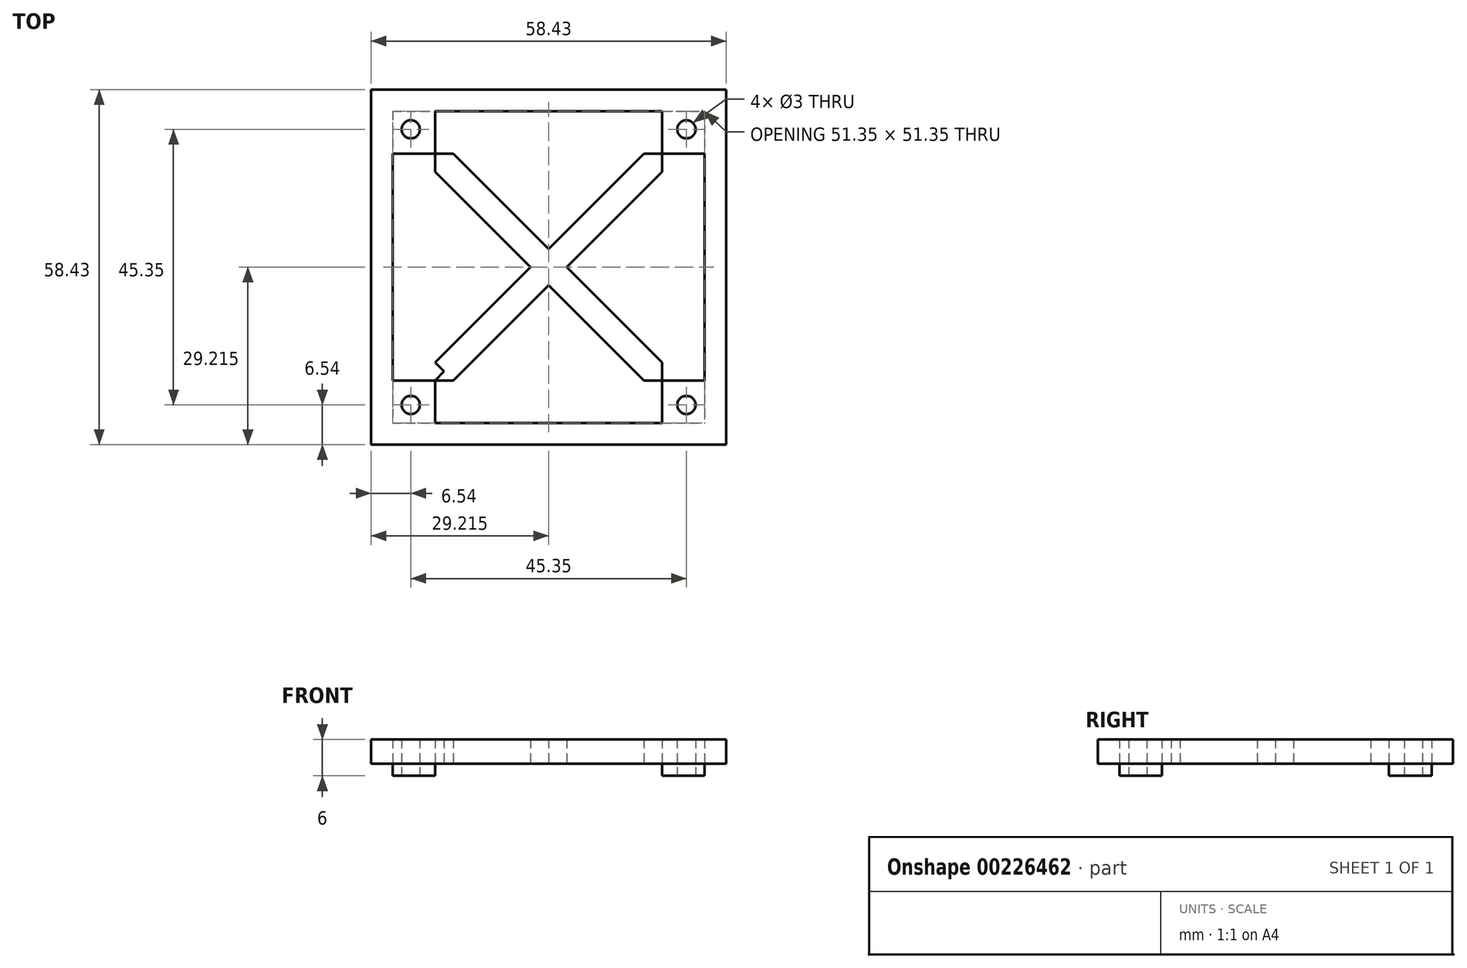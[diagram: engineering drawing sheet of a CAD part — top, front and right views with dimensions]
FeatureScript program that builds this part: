
annotation { "Feature Type Name" : "Feature", "Feature Type Description" : "" }
export const myFeature = defineFeature(function(context is Context, id is Id, definition is map)
    precondition{}
    {
        {
            var Q0;
            Q0=qCreatedBy(makeId("Top.planeOp"),FACE);
            var sketch = newSketch(context, id + "F0", { "sketchPlane" : qUnion([Q0])});
            skLineSegment(sketch, "E0.bottom", {"start": v(0, 0) * mm, "end": v(51.35, 0) * mm});
            skLineSegment(sketch, "E0.top", {"start": v(0, -51.35) * mm, "end": v(51.35, -51.35) * mm});
            skLineSegment(sketch, "E0.left", {"start": v(0, 0) * mm, "end": v(0, -51.35) * mm});
            skLineSegment(sketch, "E0.right", {"start": v(51.35, 0) * mm, "end": v(51.35, -51.35) * mm});
            skCircle(sketch, "E1", {"center": v(3, -3) * mm, "radius": 1.5 * mm});
            skCircle(sketch, "E2", {"center": v(48.35, -3) * mm, "radius": 1.5 * mm});
            skCircle(sketch, "E3", {"center": v(48.35, -48.35) * mm, "radius": 1.5 * mm});
            skCircle(sketch, "E4", {"center": v(3, -48.35) * mm, "radius": 1.5 * mm});
            skLineSegment(sketch, "E5", {"start": v(0, -3) * mm, "end": v(1.5, -3) * mm});
            skLineSegment(sketch, "E6", {"start": v(51.35, -3) * mm, "end": v(49.85, -3) * mm});
            skLineSegment(sketch, "E7", {"start": v(3, -1.5) * mm, "end": v(3, 0) * mm});
            skLineSegment(sketch, "E8", {"start": v(3, -51.35) * mm, "end": v(3, -48.35) * mm});
            skLineSegment(sketch, "E9", {"start": v(3, -48.35) * mm, "end": v(0, -48.35) * mm});
            skLineSegment(sketch, "E10", {"start": v(48.35, -48.35) * mm, "end": v(51.35, -48.35) * mm});
            skLineSegment(sketch, "E11", {"start": v(48.35, -48.35) * mm, "end": v(48.35, -51.35) * mm});
            skLineSegment(sketch, "E12", {"start": v(1.5, -3) * mm, "end": v(3, -3) * mm});
            skLineSegment(sketch, "E13", {"start": v(3, -3) * mm, "end": v(3, -1.5) * mm});
            skLineSegment(sketch, "E14", {"start": v(48.35, -3) * mm, "end": v(49.85, -3) * mm});
            skLineSegment(sketch, "E15", {"start": v(48.35, -3) * mm, "end": v(48.35, 0) * mm});
            skLineSegment(sketch, "E16", {"start": v(3, -3) * mm, "end": v(0, 0) * mm});
            skLineSegment(sketch, "E17", {"start": v(0, 0) * mm, "end": v(-3.54, 3.54) * mm});
            skLineSegment(sketch, "E18", {"start": v(51.35, 0) * mm, "end": v(54.89, 3.54) * mm});
            skLineSegment(sketch, "E19", {"start": v(51.35, -51.35) * mm, "end": v(54.89, -54.89) * mm});
            skLineSegment(sketch, "E20", {"start": v(54.89, -54.89) * mm, "end": v(-3.54, -54.89) * mm});
            skLineSegment(sketch, "E21", {"start": v(-3.54, -54.89) * mm, "end": v(0, -51.35) * mm});
            skLineSegment(sketch, "E22", {"start": v(-3.54, -54.89) * mm, "end": v(-3.54, 3.54) * mm});
            skLineSegment(sketch, "E23", {"start": v(54.89, 3.54) * mm, "end": v(-3.54, 3.54) * mm});
            skLineSegment(sketch, "E24", {"start": v(54.89, 3.54) * mm, "end": v(54.89, -54.89) * mm});
            skLineSegment(sketch, "E25.bottom", {"start": v(0, -51.35) * mm, "end": v(7, -51.35) * mm});
            skLineSegment(sketch, "E25.top", {"start": v(0, -44.35) * mm, "end": v(7, -44.35) * mm});
            skLineSegment(sketch, "E25.left", {"start": v(0, -51.35) * mm, "end": v(0, -44.35) * mm});
            skLineSegment(sketch, "E25.right", {"start": v(7, -51.35) * mm, "end": v(7, -44.35) * mm});
            skLineSegment(sketch, "E26.bottom", {"start": v(51.35, -51.35) * mm, "end": v(44.35, -51.35) * mm});
            skLineSegment(sketch, "E26.top", {"start": v(51.35, -44.35) * mm, "end": v(44.35, -44.35) * mm});
            skLineSegment(sketch, "E26.left", {"start": v(51.35, -51.35) * mm, "end": v(51.35, -44.35) * mm});
            skLineSegment(sketch, "E26.right", {"start": v(44.35, -51.35) * mm, "end": v(44.35, -44.35) * mm});
            skLineSegment(sketch, "E27.bottom", {"start": v(51.35, 0) * mm, "end": v(44.35, 0) * mm});
            skLineSegment(sketch, "E27.top", {"start": v(51.35, -7) * mm, "end": v(44.35, -7) * mm});
            skLineSegment(sketch, "E27.left", {"start": v(51.35, 0) * mm, "end": v(51.35, -7) * mm});
            skLineSegment(sketch, "E27.right", {"start": v(44.35, 0) * mm, "end": v(44.35, -7) * mm});
            skLineSegment(sketch, "E28.bottom", {"start": v(0, 0) * mm, "end": v(7, 0) * mm});
            skLineSegment(sketch, "E28.top", {"start": v(0, -7) * mm, "end": v(7, -7) * mm});
            skLineSegment(sketch, "E28.left", {"start": v(0, 0) * mm, "end": v(0, -7) * mm});
            skLineSegment(sketch, "E28.right", {"start": v(7, 0) * mm, "end": v(7, -7) * mm});
            skLineSegment(sketch, "E29", {"start": v(7, -44.35) * mm, "end": v(7, -7) * mm});
            skLineSegment(sketch, "E30", {"start": v(44.35, -7) * mm, "end": v(7, -7) * mm});
            skLineSegment(sketch, "E31", {"start": v(44.35, -7) * mm, "end": v(44.35, -44.35) * mm});
            skLineSegment(sketch, "E32", {"start": v(44.35, -44.35) * mm, "end": v(7, -44.35) * mm});
            skLineSegment(sketch, "E33", {"start": v(7, -44.35) * mm, "end": v(44.35, -7) * mm});
            skLineSegment(sketch, "E34", {"start": v(44.35, -44.35) * mm, "end": v(7, -7) * mm});
            skLineSegment(sketch, "E35", {"start": v(10, -44.35) * mm, "end": v(44.35, -10) * mm});
            skLineSegment(sketch, "E36", {"start": v(44.35, -10) * mm, "end": v(41.35, -7) * mm});
            skLineSegment(sketch, "E37", {"start": v(41.35, -7) * mm, "end": v(7, -41.35) * mm});
            skLineSegment(sketch, "E38", {"start": v(7, -10) * mm, "end": v(41.35, -44.35) * mm});
            skLineSegment(sketch, "E39", {"start": v(41.35, -44.35) * mm, "end": v(44.35, -41.35) * mm});
            skLineSegment(sketch, "E40", {"start": v(44.35, -41.35) * mm, "end": v(10, -7) * mm});
            skLineSegment(sketch, "E41", {"start": v(10, -7) * mm, "end": v(7, -10) * mm});
            skLineSegment(sketch, "E42", {"start": v(7, -41.35) * mm, "end": v(10, -44.35) * mm});
            skLineSegment(sketch, "E43", {"start": v(42.85, -8.5) * mm, "end": v(41.35, -7) * mm});
            skLineSegment(sketch, "E44", {"start": v(7, -41.35) * mm, "end": v(7, -44.35) * mm});
            skSolve(sketch);
        }
        {
            var Q0;
            {var subQ2=sQuery(id+"F0.wireOp",EDGE,"E0.top");Q0=makeQuery(id+"F0.imprint","IMPRINT",FACE,{"disambiguationData":[TD([[makeQuery(id+"F0.imprint","IMPRINT",EDGE,{"derivedFrom":subQ2}),-1.0]])]});}
            var Q1;
            Q1=makeQuery(id+"F0.imprint","IMPRINT",FACE,{"disambiguationData":[TD([[makeQuery(id+"F0.imprint","IMPRINT",EDGE,{"derivedFrom":sQuery(id+"F0.wireOp",EDGE,"E0.left")}),1.0]])]});
            var Q2;
            Q2=makeQuery(id+"F0.imprint","IMPRINT",FACE,{"disambiguationData":[TD([[makeQuery(id+"F0.imprint","IMPRINT",EDGE,{"derivedFrom":sQuery(id+"F0.wireOp",EDGE,"E0.top")}),1.0]])]});
            var Q3;
            {var subQ9=sQuery(id+"F0.wireOp",EDGE,"E25.top");Q3=makeQuery(id+"F0.imprint","IMPRINT",FACE,{"disambiguationData":[TD([[makeQuery(id+"F0.imprint","IMPRINT",EDGE,{"derivedFrom":subQ9}),-1.0]])]});}
            var Q4;
            {var subQ1=sQuery(id+"F0.wireOp",EDGE,"E8");var subQ7=sQuery(id+"F0.wireOp",EDGE,"E4");var subQ9=makeQuery(id+"F0.imprint","INTERSECT",VERTEX,{"derivedFrom":[subQ7,subQ1]});Q4=makeQuery(id+"F0.imprint","IMPRINT",FACE,{"disambiguationData":[TD([[makeQuery(id+"F0.imprint","IMPRINT",EDGE,{"disambiguationData":[TD([[subQ9,1.0]])],"derivedFrom":subQ7}),-1.0]])]});}
            var Q5;
            {var subQ1=sQuery(id+"F0.wireOp",EDGE,"E0.left");Q5=makeQuery(id+"F0.imprint","IMPRINT",FACE,{"disambiguationData":[TD([[makeQuery(id+"F0.imprint","IMPRINT",EDGE,{"derivedFrom":subQ1}),-1.0]])]});}
            var Q6;
            {var subQ4=sQuery(id+"F0.wireOp",EDGE,"E5");Q6=makeQuery(id+"F0.imprint","IMPRINT",FACE,{"disambiguationData":[TD([[makeQuery(id+"F0.imprint","IMPRINT",EDGE,{"derivedFrom":subQ4}),-1.0]])]});}
            var Q7;
            {var subQ0=sQuery(id+"F0.wireOp",EDGE,"E7");Q7=makeQuery(id+"F0.imprint","IMPRINT",FACE,{"disambiguationData":[TD([[makeQuery(id+"F0.imprint","IMPRINT",EDGE,{"derivedFrom":subQ0}),1.0]])]});}
            var Q8;
            {var subQ0=sQuery(id+"F0.wireOp",EDGE,"E5");Q8=makeQuery(id+"F0.imprint","IMPRINT",FACE,{"disambiguationData":[TD([[makeQuery(id+"F0.imprint","IMPRINT",EDGE,{"derivedFrom":subQ0}),1.0]])]});}
            var Q9;
            {var subQ2=sQuery(id+"F0.wireOp",EDGE,"E0.bottom");Q9=makeQuery(id+"F0.imprint","IMPRINT",FACE,{"disambiguationData":[TD([[makeQuery(id+"F0.imprint","IMPRINT",EDGE,{"derivedFrom":subQ2}),1.0]])]});}
            var Q10;
            Q10=makeQuery(id+"F0.imprint","IMPRINT",FACE,{"disambiguationData":[TD([[makeQuery(id+"F0.imprint","IMPRINT",EDGE,{"derivedFrom":sQuery(id+"F0.wireOp",EDGE,"E0.bottom")}),-1.0]])]});
            var Q11;
            {var subQ4=sQuery(id+"F0.wireOp",EDGE,"E6");Q11=makeQuery(id+"F0.imprint","IMPRINT",FACE,{"disambiguationData":[TD([[makeQuery(id+"F0.imprint","IMPRINT",EDGE,{"derivedFrom":subQ4}),1.0]])]});}
            var Q12;
            {var subQ5=sQuery(id+"F0.wireOp",EDGE,"E6");Q12=makeQuery(id+"F0.imprint","IMPRINT",FACE,{"disambiguationData":[TD([[makeQuery(id+"F0.imprint","IMPRINT",EDGE,{"derivedFrom":subQ5}),-1.0]])]});}
            var Q13;
            {var subQ4=sQuery(id+"F0.wireOp",EDGE,"E0.right");Q13=makeQuery(id+"F0.imprint","IMPRINT",FACE,{"disambiguationData":[TD([[makeQuery(id+"F0.imprint","IMPRINT",EDGE,{"derivedFrom":subQ4}),1.0]])]});}
            var Q14;
            Q14=makeQuery(id+"F0.imprint","IMPRINT",FACE,{"disambiguationData":[TD([[makeQuery(id+"F0.imprint","IMPRINT",EDGE,{"derivedFrom":sQuery(id+"F0.wireOp",EDGE,"E0.right")}),-1.0]])]});
            var Q15;
            {var subQ3=sQuery(id+"F0.wireOp",EDGE,"E3");var subQ7=sQuery(id+"F0.wireOp",EDGE,"E10");var subQ9=makeQuery(id+"F0.imprint","INTERSECT",VERTEX,{"derivedFrom":[subQ3,subQ7]});Q15=makeQuery(id+"F0.imprint","IMPRINT",FACE,{"disambiguationData":[TD([[makeQuery(id+"F0.imprint","IMPRINT",EDGE,{"disambiguationData":[TD([[subQ9,1.0]])],"derivedFrom":subQ3}),-1.0]])]});}
            var Q16;
            {var subQ10=sQuery(id+"F0.wireOp",EDGE,"E26.top");Q16=makeQuery(id+"F0.imprint","IMPRINT",FACE,{"disambiguationData":[TD([[makeQuery(id+"F0.imprint","IMPRINT",EDGE,{"derivedFrom":subQ10}),1.0]])]});}
            var Q17;
            {var subQ0=sQuery(id+"F0.wireOp",EDGE,"E44");Q17=makeQuery(id+"F0.imprint","IMPRINT",FACE,{"disambiguationData":[TD([[makeQuery(id+"F0.imprint","IMPRINT",EDGE,{"derivedFrom":subQ0}),1.0]])]});}
            var Q18;
            {var subQ0=sQuery(id+"F0.wireOp",EDGE,"E33");var subQ3=sQuery(id+"F0.wireOp",EDGE,"E42");var subQ5=makeQuery(id+"F0.imprint","INTERSECT",VERTEX,{"derivedFrom":[subQ0,subQ3]});Q18=makeQuery(id+"F0.imprint","IMPRINT",FACE,{"disambiguationData":[TD([[makeQuery(id+"F0.imprint","IMPRINT",EDGE,{"disambiguationData":[TD([[subQ5,-1.0]])],"derivedFrom":subQ3}),-1.0]])]});}
            var Q19;
            {var subQ0=sQuery(id+"F0.wireOp",EDGE,"E42");var subQ1=sQuery(id+"F0.wireOp",EDGE,"E33");var subQ2=makeQuery(id+"F0.imprint","INTERSECT",VERTEX,{"derivedFrom":[subQ1,subQ0]});Q19=makeQuery(id+"F0.imprint","IMPRINT",FACE,{"disambiguationData":[TD([[makeQuery(id+"F0.imprint","IMPRINT",EDGE,{"disambiguationData":[TD([[subQ2,-1.0]])],"derivedFrom":subQ1}),-1.0]])]});}
            var Q20;
            {var subQ0=sQuery(id+"F0.wireOp",EDGE,"E42");var subQ1=sQuery(id+"F0.wireOp",EDGE,"E33");var subQ2=makeQuery(id+"F0.imprint","INTERSECT",VERTEX,{"derivedFrom":[subQ1,subQ0]});Q20=makeQuery(id+"F0.imprint","IMPRINT",FACE,{"disambiguationData":[TD([[makeQuery(id+"F0.imprint","IMPRINT",EDGE,{"disambiguationData":[TD([[subQ2,-1.0]])],"derivedFrom":subQ1}),1.0]])]});}
            var Q21;
            {var subQ0=sQuery(id+"F0.wireOp",EDGE,"E37");var subQ1=sQuery(id+"F0.wireOp",EDGE,"E34");var subQ2=makeQuery(id+"F0.imprint","INTERSECT",VERTEX,{"derivedFrom":[subQ1,subQ0]});Q21=makeQuery(id+"F0.imprint","IMPRINT",FACE,{"disambiguationData":[TD([[makeQuery(id+"F0.imprint","IMPRINT",EDGE,{"disambiguationData":[TD([[subQ2,-1.0]])],"derivedFrom":subQ1}),1.0]])]});}
            var Q22;
            {var subQ0=sQuery(id+"F0.wireOp",EDGE,"E37");var subQ1=sQuery(id+"F0.wireOp",EDGE,"E34");var subQ2=makeQuery(id+"F0.imprint","INTERSECT",VERTEX,{"derivedFrom":[subQ1,subQ0]});Q22=makeQuery(id+"F0.imprint","IMPRINT",FACE,{"disambiguationData":[TD([[makeQuery(id+"F0.imprint","IMPRINT",EDGE,{"disambiguationData":[TD([[subQ2,-1.0]])],"derivedFrom":subQ1}),-1.0]])]});}
            var Q23;
            {var subQ0=sQuery(id+"F0.wireOp",EDGE,"E34");var subQ1=sQuery(id+"F0.wireOp",EDGE,"E33");var subQ2=makeQuery(id+"F0.imprint","INTERSECT",VERTEX,{"derivedFrom":[subQ1,subQ0]});Q23=makeQuery(id+"F0.imprint","IMPRINT",FACE,{"disambiguationData":[TD([[makeQuery(id+"F0.imprint","IMPRINT",EDGE,{"disambiguationData":[TD([[subQ2,-1.0]])],"derivedFrom":subQ1}),1.0]])]});}
            var Q24;
            {var subQ0=sQuery(id+"F0.wireOp",EDGE,"E34");var subQ1=sQuery(id+"F0.wireOp",EDGE,"E33");var subQ2=makeQuery(id+"F0.imprint","INTERSECT",VERTEX,{"derivedFrom":[subQ1,subQ0]});Q24=makeQuery(id+"F0.imprint","IMPRINT",FACE,{"disambiguationData":[TD([[makeQuery(id+"F0.imprint","IMPRINT",EDGE,{"disambiguationData":[TD([[subQ2,-1.0]])],"derivedFrom":subQ1}),-1.0]])]});}
            var Q25;
            {var subQ0=sQuery(id+"F0.wireOp",EDGE,"E38");var subQ1=sQuery(id+"F0.wireOp",EDGE,"E33");var subQ2=makeQuery(id+"F0.imprint","INTERSECT",VERTEX,{"derivedFrom":[subQ1,subQ0]});Q25=makeQuery(id+"F0.imprint","IMPRINT",FACE,{"disambiguationData":[TD([[makeQuery(id+"F0.imprint","IMPRINT",EDGE,{"disambiguationData":[TD([[subQ2,-1.0]])],"derivedFrom":subQ1}),-1.0]])]});}
            var Q26;
            {var subQ0=sQuery(id+"F0.wireOp",EDGE,"E38");var subQ1=sQuery(id+"F0.wireOp",EDGE,"E33");var subQ2=makeQuery(id+"F0.imprint","INTERSECT",VERTEX,{"derivedFrom":[subQ1,subQ0]});Q26=makeQuery(id+"F0.imprint","IMPRINT",FACE,{"disambiguationData":[TD([[makeQuery(id+"F0.imprint","IMPRINT",EDGE,{"disambiguationData":[TD([[subQ2,-1.0]])],"derivedFrom":subQ1}),1.0]])]});}
            var Q27;
            {var subQ0=sQuery(id+"F0.wireOp",EDGE,"E39");var subQ1=sQuery(id+"F0.wireOp",EDGE,"E34");var subQ2=makeQuery(id+"F0.imprint","INTERSECT",VERTEX,{"derivedFrom":[subQ1,subQ0]});Q27=makeQuery(id+"F0.imprint","IMPRINT",FACE,{"disambiguationData":[TD([[makeQuery(id+"F0.imprint","IMPRINT",EDGE,{"disambiguationData":[TD([[subQ2,-1.0]])],"derivedFrom":subQ1}),1.0]])]});}
            var Q28;
            {var subQ0=sQuery(id+"F0.wireOp",EDGE,"E39");var subQ1=sQuery(id+"F0.wireOp",EDGE,"E34");var subQ2=makeQuery(id+"F0.imprint","INTERSECT",VERTEX,{"derivedFrom":[subQ1,subQ0]});Q28=makeQuery(id+"F0.imprint","IMPRINT",FACE,{"disambiguationData":[TD([[makeQuery(id+"F0.imprint","IMPRINT",EDGE,{"disambiguationData":[TD([[subQ2,-1.0]])],"derivedFrom":subQ1}),-1.0]])]});}
            var Q29;
            {var subQ0=sQuery(id+"F0.wireOp",EDGE,"E34");var subQ3=sQuery(id+"F0.wireOp",EDGE,"E41");var subQ5=makeQuery(id+"F0.imprint","INTERSECT",VERTEX,{"derivedFrom":[subQ0,subQ3]});Q29=makeQuery(id+"F0.imprint","IMPRINT",FACE,{"disambiguationData":[TD([[makeQuery(id+"F0.imprint","IMPRINT",EDGE,{"disambiguationData":[TD([[subQ5,-1.0]])],"derivedFrom":subQ3}),-1.0]])]});}
            var Q30;
            {var subQ0=sQuery(id+"F0.wireOp",EDGE,"E34");var subQ3=sQuery(id+"F0.wireOp",EDGE,"E41");var subQ5=makeQuery(id+"F0.imprint","INTERSECT",VERTEX,{"derivedFrom":[subQ0,subQ3]});Q30=makeQuery(id+"F0.imprint","IMPRINT",FACE,{"disambiguationData":[TD([[makeQuery(id+"F0.imprint","IMPRINT",EDGE,{"disambiguationData":[TD([[subQ5,1.0]])],"derivedFrom":subQ3}),-1.0]])]});}
            var Q31;
            {var subQ0=sQuery(id+"F0.wireOp",EDGE,"E36");Q31=makeQuery(id+"F0.imprint","IMPRINT",FACE,{"disambiguationData":[TD([[makeQuery(id+"F0.imprint","IMPRINT",EDGE,{"derivedFrom":subQ0}),1.0]])]});}
            var Q32;
            {var subQ0=sQuery(id+"F0.wireOp",EDGE,"E43");Q32=makeQuery(id+"F0.imprint","IMPRINT",FACE,{"disambiguationData":[TD([[makeQuery(id+"F0.imprint","IMPRINT",EDGE,{"derivedFrom":subQ0}),1.0]])]});}
            var Q33;
            {var subQ3=sQuery(id+"F0.wireOp",EDGE,"E36");Q33=makeQuery(id+"F0.imprint","IMPRINT",FACE,{"disambiguationData":[TD([[makeQuery(id+"F0.imprint","IMPRINT",EDGE,{"derivedFrom":subQ3}),-1.0]])]});}
            var Q34;
            {var subQ0=sQuery(id+"F0.wireOp",EDGE,"E34");var subQ3=sQuery(id+"F0.wireOp",EDGE,"E39");var subQ5=makeQuery(id+"F0.imprint","INTERSECT",VERTEX,{"derivedFrom":[subQ0,subQ3]});Q34=makeQuery(id+"F0.imprint","IMPRINT",FACE,{"disambiguationData":[TD([[makeQuery(id+"F0.imprint","IMPRINT",EDGE,{"disambiguationData":[TD([[subQ5,-1.0]])],"derivedFrom":subQ3}),-1.0]])]});}
            var Q35;
            {var subQ0=sQuery(id+"F0.wireOp",EDGE,"E34");var subQ3=sQuery(id+"F0.wireOp",EDGE,"E39");var subQ5=makeQuery(id+"F0.imprint","INTERSECT",VERTEX,{"derivedFrom":[subQ0,subQ3]});Q35=makeQuery(id+"F0.imprint","IMPRINT",FACE,{"disambiguationData":[TD([[makeQuery(id+"F0.imprint","IMPRINT",EDGE,{"disambiguationData":[TD([[subQ5,1.0]])],"derivedFrom":subQ3}),-1.0]])]});}
            var Q36;
            {var subQ3=sQuery(id+"F0.wireOp",EDGE,"E43");Q36=makeQuery(id+"F0.imprint","IMPRINT",FACE,{"disambiguationData":[TD([[makeQuery(id+"F0.imprint","IMPRINT",EDGE,{"derivedFrom":subQ3}),-1.0]])]});}
            extrude(context, id + "F1", {"entities" : qUnion([Q0, Q1, Q2, Q3, Q4, Q5, Q6, Q7, Q8, Q9, Q10, Q11, Q12, Q13, Q14, Q15, Q16, Q17, Q18, Q19, Q20, Q21, Q22, Q23, Q24, Q25, Q26, Q27, Q28, Q29, Q30, Q31, Q32, Q33, Q34, Q35, Q36]), "depth" : 4 * mm});
        }
        {
            var Q0;
            {var subQ9=sQuery(id+"F0.wireOp",EDGE,"E25.top");Q0=makeQuery(id+"F0.imprint","IMPRINT",FACE,{"disambiguationData":[TD([[makeQuery(id+"F0.imprint","IMPRINT",EDGE,{"derivedFrom":subQ9}),-1.0]])]});}
            var Q1;
            {var subQ1=sQuery(id+"F0.wireOp",EDGE,"E8");var subQ7=sQuery(id+"F0.wireOp",EDGE,"E4");var subQ9=makeQuery(id+"F0.imprint","INTERSECT",VERTEX,{"derivedFrom":[subQ7,subQ1]});Q1=makeQuery(id+"F0.imprint","IMPRINT",FACE,{"disambiguationData":[TD([[makeQuery(id+"F0.imprint","IMPRINT",EDGE,{"disambiguationData":[TD([[subQ9,1.0]])],"derivedFrom":subQ7}),-1.0]])]});}
            var Q2;
            {var subQ10=sQuery(id+"F0.wireOp",EDGE,"E26.top");Q2=makeQuery(id+"F0.imprint","IMPRINT",FACE,{"disambiguationData":[TD([[makeQuery(id+"F0.imprint","IMPRINT",EDGE,{"derivedFrom":subQ10}),1.0]])]});}
            var Q3;
            {var subQ3=sQuery(id+"F0.wireOp",EDGE,"E3");var subQ7=sQuery(id+"F0.wireOp",EDGE,"E10");var subQ9=makeQuery(id+"F0.imprint","INTERSECT",VERTEX,{"derivedFrom":[subQ3,subQ7]});Q3=makeQuery(id+"F0.imprint","IMPRINT",FACE,{"disambiguationData":[TD([[makeQuery(id+"F0.imprint","IMPRINT",EDGE,{"disambiguationData":[TD([[subQ9,1.0]])],"derivedFrom":subQ3}),-1.0]])]});}
            var Q4;
            {var subQ4=sQuery(id+"F0.wireOp",EDGE,"E6");Q4=makeQuery(id+"F0.imprint","IMPRINT",FACE,{"disambiguationData":[TD([[makeQuery(id+"F0.imprint","IMPRINT",EDGE,{"derivedFrom":subQ4}),1.0]])]});}
            var Q5;
            {var subQ5=sQuery(id+"F0.wireOp",EDGE,"E6");Q5=makeQuery(id+"F0.imprint","IMPRINT",FACE,{"disambiguationData":[TD([[makeQuery(id+"F0.imprint","IMPRINT",EDGE,{"derivedFrom":subQ5}),-1.0]])]});}
            var Q6;
            {var subQ4=sQuery(id+"F0.wireOp",EDGE,"E5");Q6=makeQuery(id+"F0.imprint","IMPRINT",FACE,{"disambiguationData":[TD([[makeQuery(id+"F0.imprint","IMPRINT",EDGE,{"derivedFrom":subQ4}),-1.0]])]});}
            var Q7;
            {var subQ0=sQuery(id+"F0.wireOp",EDGE,"E5");Q7=makeQuery(id+"F0.imprint","IMPRINT",FACE,{"disambiguationData":[TD([[makeQuery(id+"F0.imprint","IMPRINT",EDGE,{"derivedFrom":subQ0}),1.0]])]});}
            var Q8;
            {var subQ0=sQuery(id+"F0.wireOp",EDGE,"E7");Q8=makeQuery(id+"F0.imprint","IMPRINT",FACE,{"disambiguationData":[TD([[makeQuery(id+"F0.imprint","IMPRINT",EDGE,{"derivedFrom":subQ0}),1.0]])]});}
            extrude(context, id + "F2", {"entities" : qUnion([Q0, Q1, Q2, Q3, Q4, Q5, Q6, Q7, Q8]), "operationType" : NewBodyOperationType.ADD, "oppositeDirection" : true, "depth" : 2 * mm});
        }
    });
